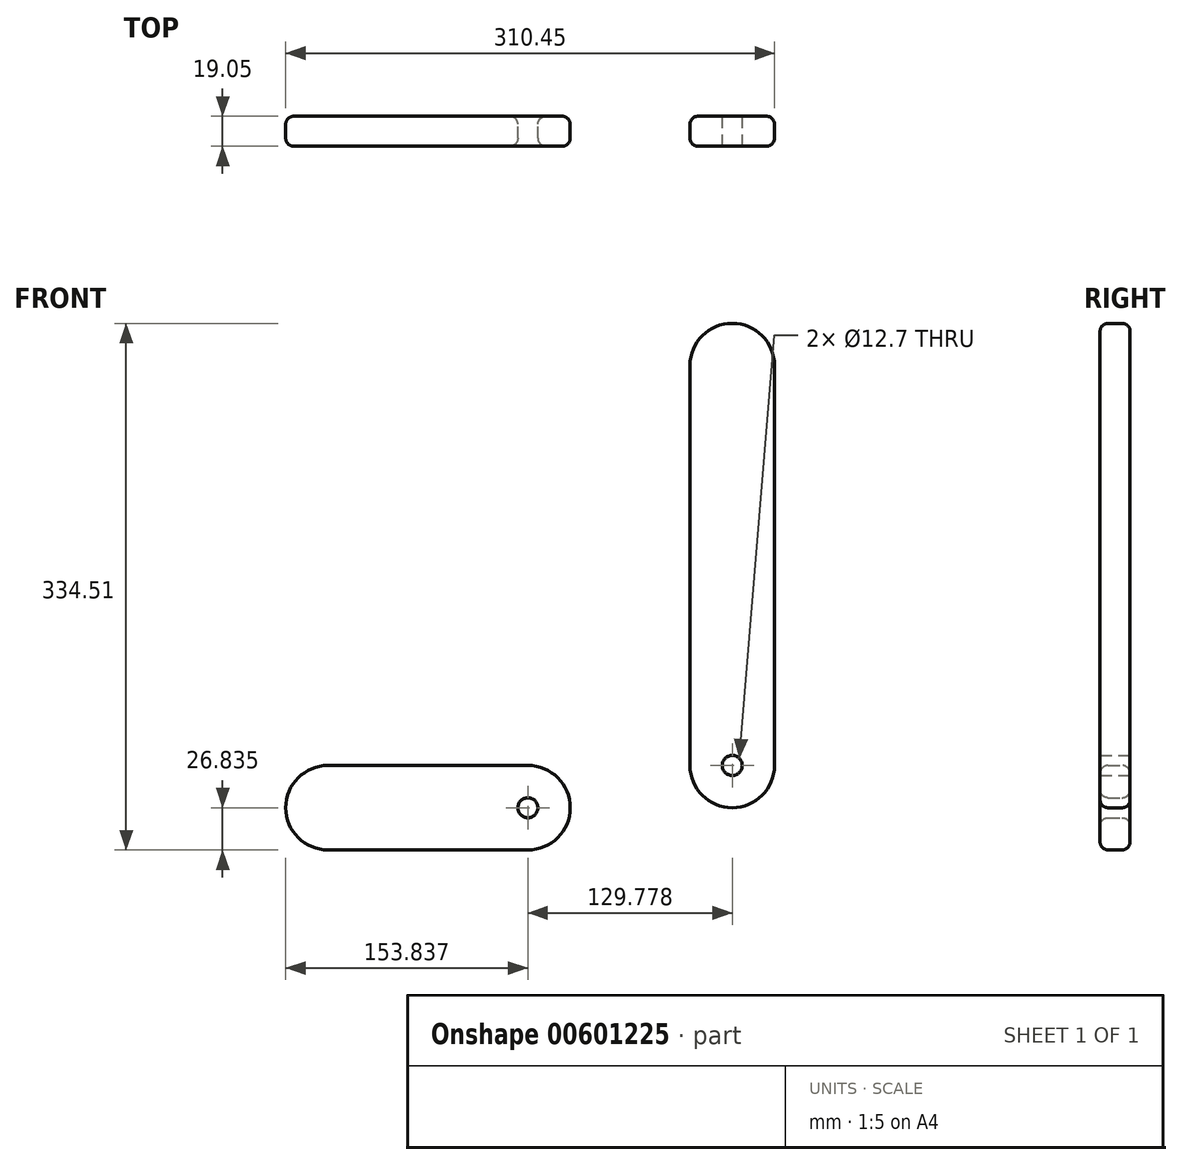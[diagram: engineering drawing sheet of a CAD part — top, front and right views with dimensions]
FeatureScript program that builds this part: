
annotation { "Feature Type Name" : "Feature", "Feature Type Description" : "" }
export const myFeature = defineFeature(function(context is Context, id is Id, definition is map)
    precondition{}
    {
        {
            var Q0;
            Q0=qCreatedBy(makeId("Front.planeOp"),FACE);
            var sketch = newSketch(context, id + "F0", { "sketchPlane" : qUnion([Q0])});
            skLineSegment(sketch, "E0", {"start": v(53.67, 0) * mm, "end": v(53.67, 254) * mm});
            skArc(sketch, "E1", {"start": v(53.67, 254) * mm, "mid": v(26.84, 280.84) * mm, "end": v(0, 254) * mm});
            skLineSegment(sketch, "E2", {"start": v(0, 254) * mm, "end": v(0, 0) * mm});
            skArc(sketch, "E3", {"start": v(0, 0) * mm, "mid": v(26.84, -26.84) * mm, "end": v(53.67, 0) * mm});
            skCircle(sketch, "E4", {"center": v(26.84, 0) * mm, "radius": 6.35 * mm});
            skSolve(sketch);
        }
        {
            var Q0;
            Q0=qCreatedBy(makeId("Front.planeOp"),FACE);
            var sketch = newSketch(context, id + "F1", { "sketchPlane" : qUnion([Q0])});
            skLineSegment(sketch, "E5", {"start": v(-102.94, -53.67) * mm, "end": v(-229.94, -53.67) * mm});
            skArc(sketch, "E6", {"start": v(-229.94, 0) * mm, "mid": v(-256.78, -26.83) * mm, "end": v(-229.94, -53.67) * mm});
            skLineSegment(sketch, "E7", {"start": v(-102.94, 0) * mm, "end": v(-229.94, 0) * mm});
            skArc(sketch, "E8", {"start": v(-102.94, -53.67) * mm, "mid": v(-76.1, -26.83) * mm, "end": v(-102.94, 0) * mm});
            skCircle(sketch, "E9", {"center": v(-102.94, -26.83) * mm, "radius": 6.35 * mm});
            skSolve(sketch);
        }
        {
            var Q0;
            Q0=makeQuery(id+"F1.imprint","IMPRINT",FACE,{"disambiguationData":[TD([[makeQuery(id+"F1.imprint","IMPRINT",EDGE,{"derivedFrom":sQuery(id+"F1.wireOp",EDGE,"E5")}),-1.0]])]});
            extrude(context, id + "F2", {"entities" : qUnion([Q0]), "depth" : 19.05 * mm, "offsetDistance" : 25.4 * mm});
        }
        {
            var Q0;
            Q0=makeQuery(id+"F0.imprint","IMPRINT",FACE,{"disambiguationData":[TD([[makeQuery(id+"F0.imprint","IMPRINT",EDGE,{"derivedFrom":sQuery(id+"F0.wireOp",EDGE,"E0")}),1.0]])]});
            extrude(context, id + "F3", {"entities" : qUnion([Q0]), "depth" : 19.05 * mm, "offsetDistance" : 25.4 * mm});
        }
        {
            var Q0;
            Q0=makeQuery(id+"F3.opExtrude","CAP_EDGE",EDGE,{"disambiguationData":[OSD([sQuery(id+"F0.wireOp",EDGE,"E2")])],"isStart":false});
            var Q1;
            Q1=makeQuery(id+"F3.opExtrude","CAP_EDGE",EDGE,{"disambiguationData":[OSD([sQuery(id+"F0.wireOp",EDGE,"E0")])],"isStart":true});
            var Q2;
            Q2=makeQuery(id+"F3.opExtrude","CAP_EDGE",EDGE,{"disambiguationData":[OSD([sQuery(id+"F0.wireOp",EDGE,"E0")])],"isStart":false});
            var Q3;
            Q3=makeQuery(id+"F3.opExtrude","CAP_EDGE",EDGE,{"disambiguationData":[OSD([sQuery(id+"F0.wireOp",EDGE,"E2")])],"isStart":true});
            fillet(context, id + "F4", {"entities" : qUnion([Q0, Q1, Q2, Q3]), "radius" : 5.08 * mm, "tangentPropagation" : true, "allowEdgeOverflow" : false});
        }
        {
            var Q0;
            Q0=makeQuery(id+"F2.opExtrude","CAP_FACE",FACE,{"disambiguationData":[OSD([sQuery(id+"F1.wireOp",EDGE,"E5"),sQuery(id+"F1.wireOp",EDGE,"E6"),sQuery(id+"F1.wireOp",EDGE,"E7"),sQuery(id+"F1.wireOp",EDGE,"E8"),sQuery(id+"F1.wireOp",EDGE,"E9")])],"isStart":false});
            var Q1;
            Q1=makeQuery(id+"F2.opExtrude","CAP_FACE",FACE,{"disambiguationData":[OSD([sQuery(id+"F1.wireOp",EDGE,"E5"),sQuery(id+"F1.wireOp",EDGE,"E6"),sQuery(id+"F1.wireOp",EDGE,"E7"),sQuery(id+"F1.wireOp",EDGE,"E8"),sQuery(id+"F1.wireOp",EDGE,"E9")])],"isStart":true});
            fillet(context, id + "F5", {"entities" : qUnion([Q0, Q1]), "radius" : 5.08 * mm, "tangentPropagation" : true, "allowEdgeOverflow" : false});
        }
    });
